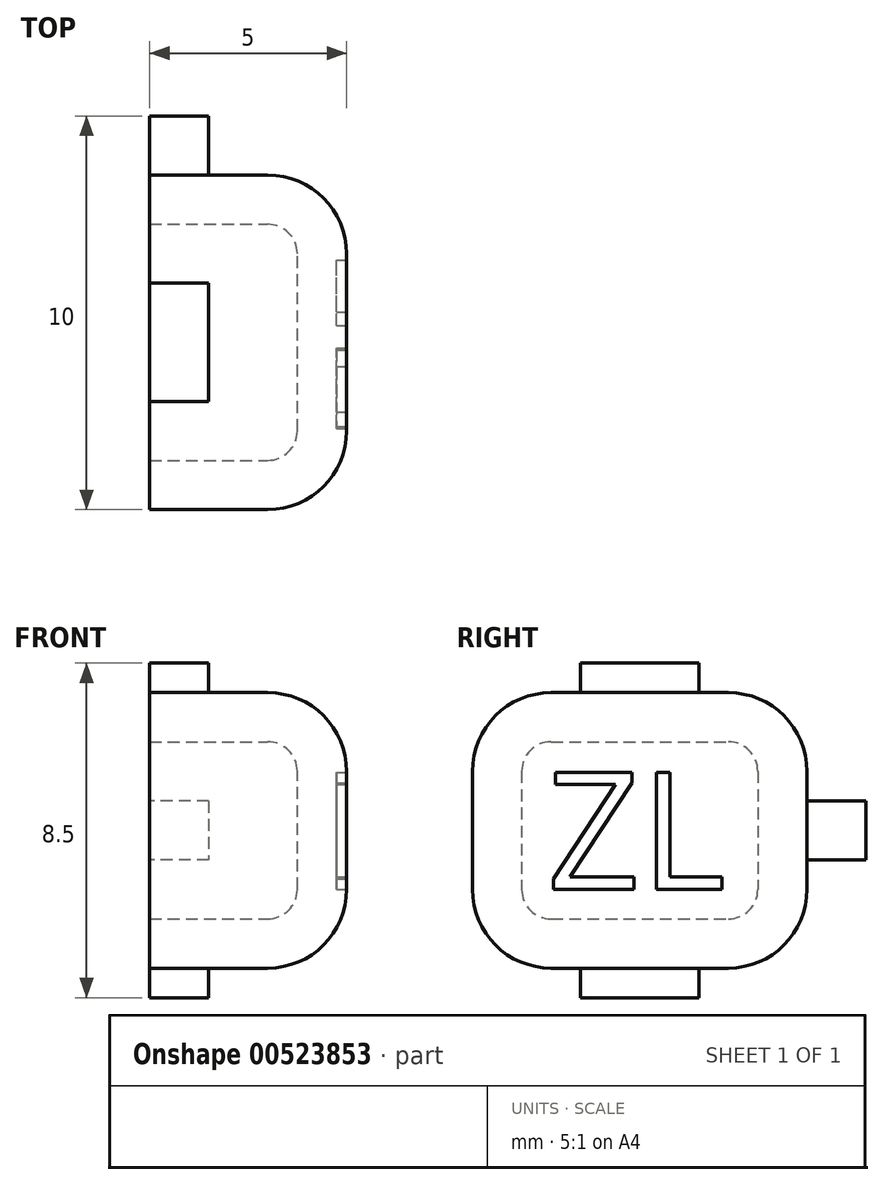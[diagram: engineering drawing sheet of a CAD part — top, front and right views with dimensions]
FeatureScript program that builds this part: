
annotation { "Feature Type Name" : "Feature", "Feature Type Description" : "" }
export const myFeature = defineFeature(function(context is Context, id is Id, definition is map)
    precondition{}
    {
        {
            var Q0;
            Q0=qCreatedBy(makeId("Right.planeOp"),FACE);
            var sketch = newSketch(context, id + "F0", { "sketchPlane" : qUnion([Q0])});
            skLineSegment(sketch, "E0.bottom", {"start": v(-4.25, 3.5) * mm, "end": v(4.25, 3.5) * mm});
            skLineSegment(sketch, "E0.top", {"start": v(-4.25, -3.5) * mm, "end": v(4.25, -3.5) * mm});
            skLineSegment(sketch, "E0.left", {"start": v(-4.25, 3.5) * mm, "end": v(-4.25, -3.5) * mm});
            skLineSegment(sketch, "E0.right", {"start": v(4.25, 3.5) * mm, "end": v(4.25, -3.5) * mm});
            skPoint(sketch, "E0.middle", {"position": v(0, 0) * mm});
            skSolve(sketch);
        }
        {
            var Q0;
            Q0=makeQuery(id+"F0.imprint","IMPRINT",FACE,{"disambiguationData":[TD([[makeQuery(id+"F0.imprint","IMPRINT",EDGE,{"derivedFrom":sQuery(id+"F0.wireOp",EDGE,"E0.bottom")}),-1.0]])]});
            extrude(context, id + "F1", {"entities" : qUnion([Q0]), "endBound" : BoundingType.SYMMETRIC, "depth" : 5 * mm, "offsetDistance" : 25 * mm});
        }
        {
            var Q0;
            Q0=makeQuery(id+"F1.opExtrude","CAP_FACE",FACE,{"disambiguationData":[OSD([sQuery(id+"F0.wireOp",EDGE,"E0.bottom"),sQuery(id+"F0.wireOp",EDGE,"E0.top"),sQuery(id+"F0.wireOp",EDGE,"E0.left"),sQuery(id+"F0.wireOp",EDGE,"E0.right")])],"isStart":false});
            var Q1;
            Q1=makeQuery(id+"F1.opExtrude","SWEPT_EDGE",EDGE,{"disambiguationData":[OSD([sQuery(id+"F0.wireOp",EDGE,"E0.bottom"),sQuery(id+"F0.wireOp",EDGE,"E0.left")])]});
            var Q2;
            Q2=makeQuery(id+"F1.opExtrude","SWEPT_EDGE",EDGE,{"disambiguationData":[OSD([sQuery(id+"F0.wireOp",EDGE,"E0.bottom"),sQuery(id+"F0.wireOp",EDGE,"E0.right")])]});
            var Q3;
            Q3=makeQuery(id+"F1.opExtrude","SWEPT_EDGE",EDGE,{"disambiguationData":[OSD([sQuery(id+"F0.wireOp",EDGE,"E0.top"),sQuery(id+"F0.wireOp",EDGE,"E0.right")])]});
            var Q4;
            Q4=makeQuery(id+"F1.opExtrude","SWEPT_EDGE",EDGE,{"disambiguationData":[OSD([sQuery(id+"F0.wireOp",EDGE,"E0.top"),sQuery(id+"F0.wireOp",EDGE,"E0.left")])]});
            fillet(context, id + "F2", {"entities" : qUnion([Q0, Q1, Q2, Q3, Q4]), "radius" : 2 * mm, "tangentPropagation" : true, "allowEdgeOverflow" : false});
        }
        {
            var Q0;
            Q0=makeQuery(id+"F1.opExtrude","CAP_FACE",FACE,{"disambiguationData":[OSD([sQuery(id+"F0.wireOp",EDGE,"E0.bottom"),sQuery(id+"F0.wireOp",EDGE,"E0.top"),sQuery(id+"F0.wireOp",EDGE,"E0.left"),sQuery(id+"F0.wireOp",EDGE,"E0.right")])],"isStart":true});
            shell(context, id + "F3", {"entities" : qUnion([Q0]), "thickness" : 1.25 * mm});
        }
        {
            var Q0;
            Q0=makeQuery(id+"F1.opExtrude","CAP_FACE",FACE,{"disambiguationData":[OSD([sQuery(id+"F0.wireOp",EDGE,"E0.bottom"),sQuery(id+"F0.wireOp",EDGE,"E0.top"),sQuery(id+"F0.wireOp",EDGE,"E0.left"),sQuery(id+"F0.wireOp",EDGE,"E0.right")])],"isStart":false});
            var sketch = newSketch(context, id + "F4", { "sketchPlane" : qUnion([Q0])});
            skText(sketch, "E1", { "text": "ZL", "fontName": "OpenSans-Regular.ttf"});
            const initialGuessF4  = {"E1": [-0.00236, -0.0015, 1, 0, 0.003]};
            skSetInitialGuess(sketch, initialGuessF4);
            skSolve(sketch);
        }
        {
            var Q0;
            Q0=qSketchRegion(id+"F4",true);
            extrude(context, id + "F5", {"entities" : qUnion([Q0]), "operationType" : NewBodyOperationType.REMOVE, "oppositeDirection" : true, "depth" : .25 * mm, "offsetDistance" : 25 * mm});
        }
        {
            var Q0;
            Q0=makeQuery(id+"F1.opExtrude","CAP_FACE",FACE,{"disambiguationData":[OSD([sQuery(id+"F0.wireOp",EDGE,"E0.bottom"),sQuery(id+"F0.wireOp",EDGE,"E0.top"),sQuery(id+"F0.wireOp",EDGE,"E0.left"),sQuery(id+"F0.wireOp",EDGE,"E0.right")])],"isStart":true});
            var sketch = newSketch(context, id + "F6", { "sketchPlane" : qUnion([Q0])});
            skLineSegment(sketch, "E2.bottom", {"start": v(1.5, 3.5) * mm, "end": v(-1.5, 3.5) * mm});
            skLineSegment(sketch, "E2.top", {"start": v(1.5, 4.25) * mm, "end": v(-1.5, 4.25) * mm});
            skLineSegment(sketch, "E2.left", {"start": v(1.5, 3.5) * mm, "end": v(1.5, 4.25) * mm});
            skLineSegment(sketch, "E2.right", {"start": v(-1.5, 3.5) * mm, "end": v(-1.5, 4.25) * mm});
            skPoint(sketch, "E2.middle", {"position": v(0, 3.87) * mm});
            skLineSegment(sketch, "E3.MirrorCS", {"start": v(1.5, -3.5) * mm, "end": v(1.5, -4.25) * mm});
            skLineSegment(sketch, "E4.MirrorCS", {"start": v(-1.5, -3.5) * mm, "end": v(-1.5, -4.25) * mm});
            skLineSegment(sketch, "E5.MirrorCS", {"start": v(1.5, -4.25) * mm, "end": v(-1.5, -4.25) * mm});
            skLineSegment(sketch, "E6.MirrorCS", {"start": v(1.5, -3.5) * mm, "end": v(-1.5, -3.5) * mm});
            skPoint(sketch, "E7.MirrorP", {"position": v(0, -3.87) * mm});
            skSolve(sketch);
        }
        {
            var Q0;
            Q0=qSketchRegion(id+"F6",true);
            extrude(context, id + "F7", {"entities" : qUnion([Q0]), "operationType" : NewBodyOperationType.ADD, "oppositeDirection" : true, "depth" : 1.5 * mm, "offsetDistance" : 25 * mm});
        }
        {
            var Q0;
            Q0=makeQuery(id+"F1.opExtrude","SWEPT_FACE",FACE,{"disambiguationData":[OSD([sQuery(id+"F0.wireOp",EDGE,"E0.right")])]});
            var sketch = newSketch(context, id + "F8", { "sketchPlane" : qUnion([Q0])});
            skLineSegment(sketch, "E8.bottom", {"start": v(1, 0.75) * mm, "end": v(2.5, 0.75) * mm});
            skLineSegment(sketch, "E8.top", {"start": v(1, -0.75) * mm, "end": v(2.5, -0.75) * mm});
            skLineSegment(sketch, "E8.left", {"start": v(1, 0.75) * mm, "end": v(1, -0.75) * mm});
            skLineSegment(sketch, "E8.right", {"start": v(2.5, 0.75) * mm, "end": v(2.5, -0.75) * mm});
            skPoint(sketch, "E8.middle", {"position": v(1.75, 0) * mm});
            skSolve(sketch);
        }
        {
            var Q0;
            Q0 = qSketchRegion(id + "F8", true);
            extrude(context, id + "F9", {"entities" : qUnion([Q0]), "operationType" : NewBodyOperationType.ADD, "depth" : 1.5 * mm, "offsetDistance" : 25 * mm});
        }
    });
